# Revit family: J 80 Buffet
name_source: partatom
category: Equipement spécialisé
revit_build: Autodesk Revit LT 2017 (Build: 20160225_1515(x64)
units: mm (PartAtom-declared; Revit-internal decimal feet)

## family parameters
Basée sur le plan de construction = Non
Cote de connecteur circulaire = Utiliser le rayon
Couper avec des vides une fois chargée = Non
Numéro OmniClass = 23.40.40.14.14.11
Partagée = Non
Point de calcul de pièce = Non
Titre OmniClass = Food Mixers
Toujours verticalement = Oui
Type d'élément = Normal

## types (4) — shared parameters
Apparent Power = 0 VA
Depth = 566 mm
Description = CENTRIFUGEUSE
Electrique connexion  Height = 10 mm  [stored 0.0328084 ft]
Electrique connexion Depth = 328 mm
Electrique connexion Width = 15 mm  [stored 0.0492126 ft]
Fabricant = ROBOT COUPE
Height = 595 mm
Modèle = J 80 Buffet
Phase = 1
Speeds (Rpm) = 3000
UP Depth = 762 mm
UP Height = 728 mm
UP Width = 465 mm
URL = www.robot-coupe.com
Weight = 12.5 kg
Width = 262 mm
water = Connector
zero-valued in all types: Cold water supply, Cold water supply height, Elec Conn RI Height, Used water, Waste water height

## per-type parameters (varying)
| type | Amps | Cycle | Volts | Watts |
| J 80 Buffet    240/50/1 | 7 | 50 Hz | 240 V | 500 W |
| J 80 Buffet    120/60/1 | 9 | 60 Hz | 120 V | 700 W |
| J 80 Buffet    220/60/1 | 6 | 60 Hz | 220 V | 500 W |
| J 80 Buffet    230/50/1 | 7 | 50 Hz | 230 V | 700 W |

note: [stored X ft] marks values corroborated as IEEE doubles in the binary element streams (Revit-internal decimal feet)

## geometry (parser evidence)
native form markers: Sweep x5
no freeform markers — native parametric forms only
